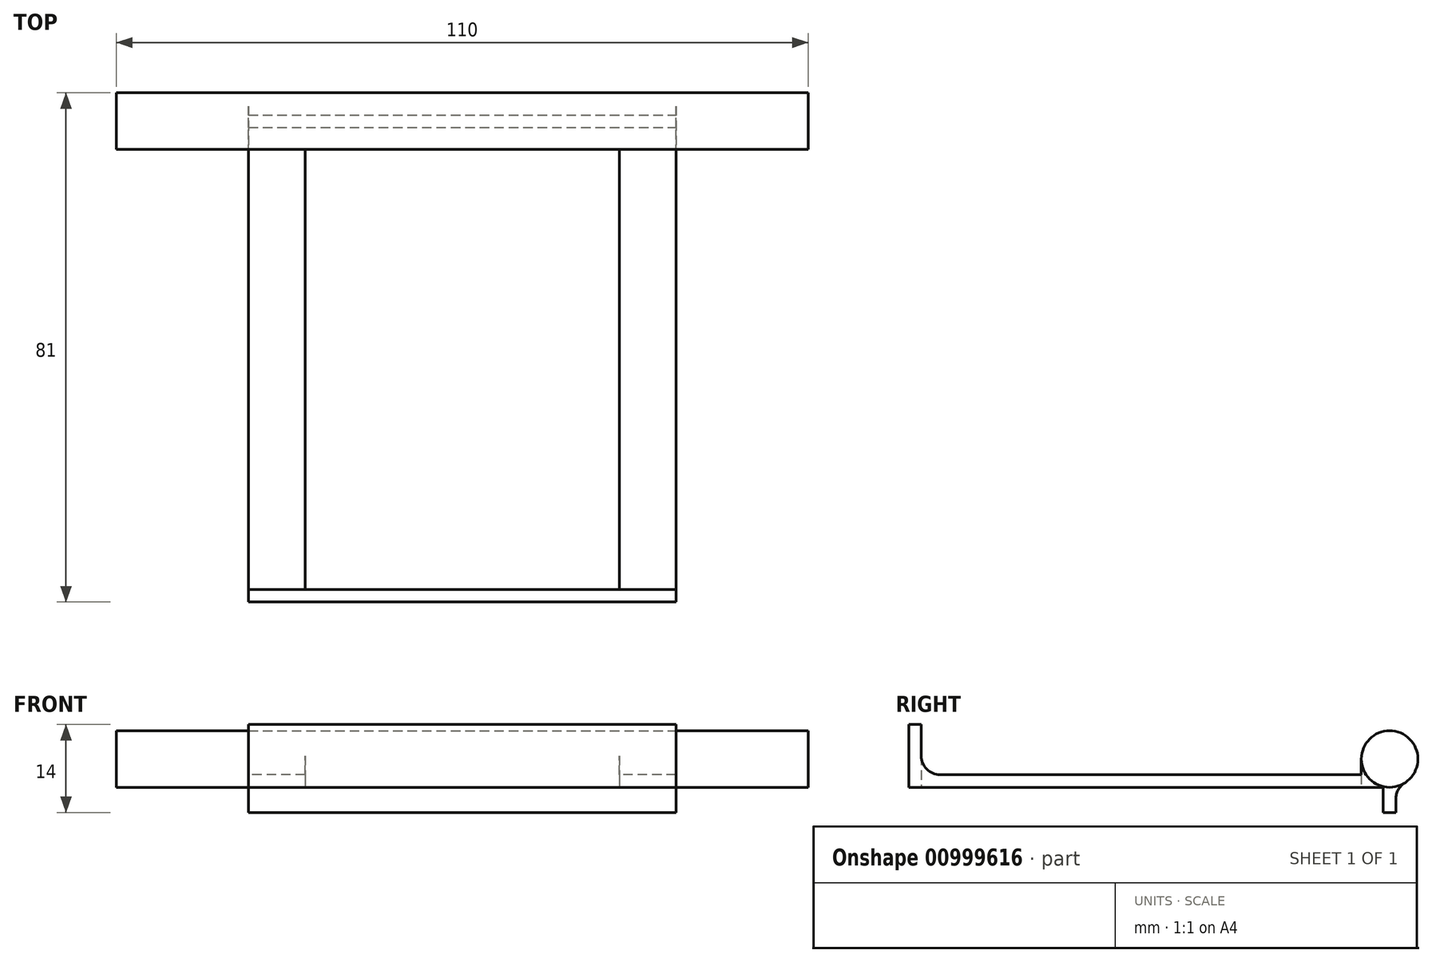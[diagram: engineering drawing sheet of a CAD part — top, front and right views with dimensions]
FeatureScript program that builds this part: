
annotation { "Feature Type Name" : "Feature", "Feature Type Description" : "" }
export const myFeature = defineFeature(function(context is Context, id is Id, definition is map)
    precondition{}
    {
        {
            var Q0;
            Q0=qCreatedBy(makeId("Top.planeOp"),FACE);
            var sketch = newSketch(context, id + "F0", { "sketchPlane" : qUnion([Q0])});
            skLineSegment(sketch, "E0.bottom", {"start": v(34, 36) * mm, "end": v(-34, 36) * mm});
            skLineSegment(sketch, "E0.top", {"start": v(34, -36) * mm, "end": v(-34, -36) * mm});
            skLineSegment(sketch, "E0.left", {"start": v(34, 36) * mm, "end": v(34, -36) * mm});
            skLineSegment(sketch, "E0.right", {"start": v(-34, 36) * mm, "end": v(-34, -36) * mm});
            skPoint(sketch, "E0.middle", {"position": v(0, 0) * mm});
            skLineSegment(sketch, "E1.bottom", {"start": v(-34, 36) * mm, "end": v(34, 36) * mm});
            skLineSegment(sketch, "E1.top", {"start": v(-34, 45) * mm, "end": v(34, 45) * mm});
            skLineSegment(sketch, "E1.left", {"start": v(-34, 36) * mm, "end": v(-34, 45) * mm});
            skLineSegment(sketch, "E1.right", {"start": v(34, 36) * mm, "end": v(34, 45) * mm});
            skLineSegment(sketch, "E2", {"start": v(-34, -34) * mm, "end": v(34, -34) * mm});
            skLineSegment(sketch, "E3.bottom", {"start": v(25, -34) * mm, "end": v(-25, -34) * mm});
            skLineSegment(sketch, "E3.left", {"start": v(25, -34) * mm, "end": v(25, 34) * mm});
            skLineSegment(sketch, "E3.right", {"start": v(-25, -34) * mm, "end": v(-25, 34) * mm});
            skLineSegment(sketch, "E4", {"start": v(25, 34) * mm, "end": v(25, 36) * mm});
            skLineSegment(sketch, "E5", {"start": v(-25, 34) * mm, "end": v(-25, 36) * mm});
            skSolve(sketch);
        }
        {
            var Q0;
            Q0=makeQuery(id+"F0.imprint","IMPRINT",FACE,{"disambiguationData":[TD([[makeQuery(id+"F0.imprint","IMPRINT",EDGE,{"derivedFrom":sQuery(id+"F0.wireOp",EDGE,"E1.top")}),-1.0]])]});
            extrude(context, id + "F1", {"entities" : qUnion([Q0]), "depth" : 9 * mm, "offsetDistance" : 25 * mm});
        }
        {
            var Q0;
            {var subQ4=sQuery(id+"F0.wireOp",EDGE,"E0.top");Q0=makeQuery(id+"F0.imprint","IMPRINT",FACE,{"disambiguationData":[TD([[makeQuery(id+"F0.imprint","IMPRINT",EDGE,{"derivedFrom":subQ4}),-1.0]])]});}
            var Q1;
            {var subQ0=sQuery(id+"F0.wireOp",EDGE,"E3.left");var subQ7=sQuery(id+"F0.wireOp",EDGE,"E3.right");Q1=qUnion([makeQuery(id+"F0.imprint","IMPRINT",FACE,{"disambiguationData":[TD([[makeQuery(id+"F0.imprint","IMPRINT",EDGE,{"derivedFrom":subQ7}),1.0]])]}),makeQuery(id+"F0.imprint","IMPRINT",FACE,{"disambiguationData":[TD([[makeQuery(id+"F0.imprint","IMPRINT",EDGE,{"derivedFrom":subQ0}),-1.0]])]})]);}
            extrude(context, id + "F2", {"entities" : qUnion([Q0, Q1]), "operationType" : NewBodyOperationType.ADD, "depth" : 2 * mm, "offsetDistance" : 25 * mm});
        }
        {
            var Q0;
            Q0=qCreatedBy(makeId("Right.planeOp"),FACE);
            var sketch = newSketch(context, id + "F3", { "sketchPlane" : qUnion([Q0])});
            skLineSegment(sketch, "E6.0.0", {"start": v(45, 0) * mm, "end": v(-36, 0) * mm});
            skLineSegment(sketch, "E6.0.1", {"start": v(-36, 0) * mm, "end": v(-36, 2) * mm});
            skLineSegment(sketch, "E6.0.2", {"start": v(-36, 2) * mm, "end": v(36, 2) * mm});
            skLineSegment(sketch, "E6.0.3", {"start": v(36, 2) * mm, "end": v(36, 9) * mm});
            skLineSegment(sketch, "E6.0.4", {"start": v(36, 9) * mm, "end": v(45, 9) * mm});
            skLineSegment(sketch, "E6.0.5", {"start": v(45, 9) * mm, "end": v(45, 0) * mm});
            skCircle(sketch, "E7", {"center": v(40.5, 4.5) * mm, "radius": 4.5 * mm});
            skPoint(sketch, "E7.centerSnap0", {"position": v(45, 4.5) * mm});
            skPoint(sketch, "E7.centerSnap1", {"position": v(40.5, 9) * mm});
            skSolve(sketch);
        }
        {
            var Q0;
            {var subQ0=sQuery(id+"F3.wireOp",EDGE,"E6.0.5");var subQ1=sQuery(id+"F3.wireOp",EDGE,"E6.0.4");var subQ2=makeQuery(id+"F3.imprint","INTERSECT",VERTEX,{"derivedFrom":[subQ1,subQ0]});Q0=makeQuery(id+"F3.imprint","IMPRINT",FACE,{"disambiguationData":[TD([[makeQuery(id+"F3.imprint","IMPRINT",EDGE,{"disambiguationData":[TD([[subQ2,1.0]])],"derivedFrom":subQ1}),-1.0]])]});}
            var Q1;
            {var subQ0=sQuery(id+"F3.wireOp",EDGE,"E6.0.5");var subQ1=sQuery(id+"F3.wireOp",EDGE,"E6.0.0");var subQ2=makeQuery(id+"F3.imprint","INTERSECT",VERTEX,{"derivedFrom":[subQ1,subQ0]});Q1=makeQuery(id+"F3.imprint","IMPRINT",FACE,{"disambiguationData":[TD([[makeQuery(id+"F3.imprint","IMPRINT",EDGE,{"disambiguationData":[TD([[subQ2,-1.0]])],"derivedFrom":subQ1}),-1.0]])]});}
            var Q2;
            {var subQ0=sQuery(id+"F3.wireOp",EDGE,"E6.0.4");var subQ1=sQuery(id+"F3.wireOp",EDGE,"E6.0.3");var subQ2=makeQuery(id+"F3.imprint","INTERSECT",VERTEX,{"derivedFrom":[subQ1,subQ0]});Q2=makeQuery(id+"F3.imprint","IMPRINT",FACE,{"disambiguationData":[TD([[makeQuery(id+"F3.imprint","IMPRINT",EDGE,{"disambiguationData":[TD([[subQ2,1.0]])],"derivedFrom":subQ1}),-1.0]])]});}
            extrude(context, id + "F4", {"entities" : qUnion([Q0, Q1, Q2]), "operationType" : NewBodyOperationType.REMOVE, "endBound" : BoundingType.SYMMETRIC, "oppositeDirection" : true, "depth" : 200 * mm, "offsetDistance" : 25 * mm});
        }
        {
            var Q0;
            {var subQ0=sQuery(id+"F3.wireOp",EDGE,"E7");var subQ1=makeQuery(id+"F3.imprint","INTERSECT",VERTEX,{"derivedFrom":[sQuery(id+"F3.wireOp",EDGE,"E6.0.4"),subQ0]});Q0=makeQuery(id+"F3.imprint","IMPRINT",FACE,{"disambiguationData":[TD([[makeQuery(id+"F3.imprint","IMPRINT",EDGE,{"disambiguationData":[TD([[subQ1,1.0]])],"derivedFrom":subQ0}),1.0]])]});}
            extrude(context, id + "F5", {"entities" : qUnion([Q0]), "operationType" : NewBodyOperationType.ADD, "endBound" : BoundingType.SYMMETRIC, "depth" : 110 * mm, "offsetDistance" : 25 * mm});
        }
        {
            var Q0;
            {var subQ4=sQuery(id+"F0.wireOp",EDGE,"E0.top");Q0=makeQuery(id+"F0.imprint","IMPRINT",FACE,{"disambiguationData":[TD([[makeQuery(id+"F0.imprint","IMPRINT",EDGE,{"derivedFrom":subQ4}),-1.0]])]});}
            extrude(context, id + "F6", {"entities" : qUnion([Q0]), "operationType" : NewBodyOperationType.ADD, "depth" : 10 * mm, "offsetDistance" : 25 * mm});
        }
        {
            var Q0;
            {var subQ0=sQuery(id+"F0.wireOp",EDGE,"E0.bottom");Q0=makeQuery(id+"F2.boolean.opBoolean","MERGE",FACE,{"derivedFrom":[makeQuery(id+"F1.opExtrude","CAP_FACE",FACE,{"disambiguationData":[OSD([subQ0,sQuery(id+"F0.wireOp",EDGE,"E1.top"),sQuery(id+"F0.wireOp",EDGE,"E1.left"),sQuery(id+"F0.wireOp",EDGE,"E1.right")])],"isStart":true}),makeQuery(id+"F2.opExtrude","CAP_FACE",FACE,{"disambiguationData":[OSD([subQ0,sQuery(id+"F0.wireOp",EDGE,"E0.top"),sQuery(id+"F0.wireOp",EDGE,"E0.left"),sQuery(id+"F0.wireOp",EDGE,"E0.right"),sQuery(id+"F0.wireOp",EDGE,"E2"),sQuery(id+"F0.wireOp",EDGE,"E3.left"),sQuery(id+"F0.wireOp",EDGE,"E3.right"),sQuery(id+"F0.wireOp",EDGE,"E4"),sQuery(id+"F0.wireOp",EDGE,"E5")])],"isStart":true})]});}
            var sketch = newSketch(context, id + "F7", { "sketchPlane" : qUnion([Q0])});
            skLineSegment(sketch, "E8.bottom", {"start": v(-34, -39.5) * mm, "end": v(34, -39.5) * mm});
            skLineSegment(sketch, "E8.top", {"start": v(-34, -41.5) * mm, "end": v(34, -41.5) * mm});
            skLineSegment(sketch, "E8.left", {"start": v(-34, -39.5) * mm, "end": v(-34, -41.5) * mm});
            skLineSegment(sketch, "E8.right", {"start": v(34, -39.5) * mm, "end": v(34, -41.5) * mm});
            skPoint(sketch, "E8.middle", {"position": v(0, -40.5) * mm});
            skSolve(sketch);
        }
        {
            var Q0;
            {var subQ0=sQuery(id+"F7.wireOp",EDGE,"E8.bottom");Q0=makeQuery(id+"F7.imprint","IMPRINT",FACE,{"disambiguationData":[TD([[makeQuery(id+"F7.imprint","IMPRINT",EDGE,{"derivedFrom":subQ0}),-1.0]])]});}
            var Q1;
            {var subQ0=sQuery(id+"F7.wireOp",EDGE,"E8.top");Q1=makeQuery(id+"F7.imprint","IMPRINT",FACE,{"disambiguationData":[TD([[makeQuery(id+"F7.imprint","IMPRINT",EDGE,{"derivedFrom":subQ0}),1.0]])]});}
            extrude(context, id + "F8", {"entities" : qUnion([Q0, Q1]), "operationType" : NewBodyOperationType.ADD, "endBound" : BoundingType.SYMMETRIC, "depth" : 8 * mm, "offsetDistance" : 25 * mm});
        }
        {
            var Q0;
            {var subQ0=sQuery(id+"F3.wireOp",EDGE,"E7");var subQ2=makeQuery(id+"F3.imprint","INTERSECT",VERTEX,{"derivedFrom":[sQuery(id+"F3.wireOp",EDGE,"E6.0.4"),subQ0]});Q0=makeQuery(id+"F8.boolean.opBoolean","INTERSECT",EDGE,{"derivedFrom":[makeQuery(id+"F5.boolean.opBoolean","MERGE",FACE,{"derivedFrom":[makeQuery(id+"F4.boolean.opBoolean","MERGE",FACE,{"derivedFrom":[],"fromTools":[makeQuery(id+"F4.opExtrude","SWEPT_FACE",FACE,{"disambiguationData":[OSD([subQ0]),TDD([makeQuery(id+"F3.imprint","IMPRINT",EDGE,{"disambiguationData":[TD([[subQ2,1.0]])],"derivedFrom":subQ0})])]}),makeQuery(id+"F4.opExtrude","SWEPT_FACE",FACE,{"disambiguationData":[OSD([subQ0]),TDD([makeQuery(id+"F3.imprint","IMPRINT",EDGE,{"disambiguationData":[TD([[makeQuery(id+"F3.imprint","INTERSECT",VERTEX,{"derivedFrom":[sQuery(id+"F3.wireOp",EDGE,"E6.0.3"),subQ0]}),1.0]])],"derivedFrom":subQ0})])]}),makeQuery(id+"F4.opExtrude","SWEPT_FACE",FACE,{"disambiguationData":[OSD([subQ0]),TDD([makeQuery(id+"F3.imprint","IMPRINT",EDGE,{"disambiguationData":[TD([[makeQuery(id+"F3.imprint","INTERSECT",VERTEX,{"derivedFrom":[sQuery(id+"F3.wireOp",EDGE,"E6.0.0"),subQ0]}),-1.0]])],"derivedFrom":subQ0})])]})]}),makeQuery(id+"F5.opExtrude","SWEPT_FACE",FACE,{"disambiguationData":[OSD([subQ0])]})]}),makeQuery(id+"F8.opExtrude","SWEPT_FACE",FACE,{"disambiguationData":[OSD([sQuery(id+"F7.wireOp",EDGE,"E8.top")])]})]});}
            var Q1;
            {var subQ0=sQuery(id+"F0.wireOp",EDGE,"E2");Q1=makeQuery(id+"F6.boolean.opBoolean","INTERSECT",EDGE,{"disambiguationData":[OD(1.0)],"derivedFrom":[makeQuery(id+"F2.opExtrude","CAP_FACE",FACE,{"disambiguationData":[OSD([sQuery(id+"F0.wireOp",EDGE,"E0.bottom"),sQuery(id+"F0.wireOp",EDGE,"E0.top"),sQuery(id+"F0.wireOp",EDGE,"E0.left"),sQuery(id+"F0.wireOp",EDGE,"E0.right"),subQ0,sQuery(id+"F0.wireOp",EDGE,"E3.left"),sQuery(id+"F0.wireOp",EDGE,"E3.right"),sQuery(id+"F0.wireOp",EDGE,"E4"),sQuery(id+"F0.wireOp",EDGE,"E5")])],"isStart":false}),makeQuery(id+"F6.opExtrude","SWEPT_FACE",FACE,{"disambiguationData":[OSD([subQ0])]})]});}
            var Q2;
            {var subQ0=sQuery(id+"F0.wireOp",EDGE,"E2");Q2=makeQuery(id+"F6.boolean.opBoolean","INTERSECT",EDGE,{"disambiguationData":[OD(0.0)],"derivedFrom":[makeQuery(id+"F2.opExtrude","CAP_FACE",FACE,{"disambiguationData":[OSD([sQuery(id+"F0.wireOp",EDGE,"E0.bottom"),sQuery(id+"F0.wireOp",EDGE,"E0.top"),sQuery(id+"F0.wireOp",EDGE,"E0.left"),sQuery(id+"F0.wireOp",EDGE,"E0.right"),subQ0,sQuery(id+"F0.wireOp",EDGE,"E3.left"),sQuery(id+"F0.wireOp",EDGE,"E3.right"),sQuery(id+"F0.wireOp",EDGE,"E4"),sQuery(id+"F0.wireOp",EDGE,"E5")])],"isStart":false}),makeQuery(id+"F6.opExtrude","SWEPT_FACE",FACE,{"disambiguationData":[OSD([subQ0])]})]});}
            fillet(context, id + "F9", {"entities" : qUnion([Q0, Q1, Q2]), "radius" : 3 * mm, "tangentPropagation" : true, "allowEdgeOverflow" : false});
        }
    });
